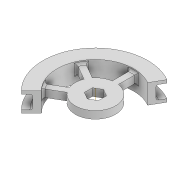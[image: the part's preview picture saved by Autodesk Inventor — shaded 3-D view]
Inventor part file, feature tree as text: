
AUTODESK INVENTOR PART (.ipt)
format: ipt  version: 2022 (Build 260153000, 153)  size: 238,080 bytes
history: native  units: mm
features: extrude x7, sketch x7, projected_geometry x4, fillet x2
ambient origin geometry x8: Origin, YZ Plane, XZ Plane, XY Plane, X Axis, Y Axis, Z Axis, Center Point
bodies: Solid1 (feature_tree)
feature tree (20):
  extrude  "Extrusion1"  Depth=44.0mm
  extrude  "Extrusion4"  Depth=4.0mm
  extrude  "Extrusion10"  Depth=1.5mm TaperAngle=0.0deg
  extrude  "Extrusion5"  Depth=20.0mm
  extrude  "Extrusion7"  Depth=1.5mm
  extrude  "Extrusion8"  Depth=10.0mm TaperAngle=0.0deg
  fillet  "Fillet1"  Radius=7.0mm
  extrude  "Extrusion9"  Depth=1.0mm
  fillet  "Fillet2"  [1 undecoded]
  sketch  "Sketch1"  dims[d0=4.1mm d1=44.0mm]
  sketch  "Sketch5"  dims[d2=3.7mm d3=0.0mm d11=4.0mm]
  projected_geometry  "Projected Loop4"
  sketch  "Sketch6"  dims[d12=1.5mm d13=0.0mm d15=1.5mm d16=0.0mm]
  projected_geometry  "Projected Loop5"
  sketch  "Sketch7"  dims[d17=3.0mm d19=20.0mm]
  projected_geometry  "Projected Loop6"
  sketch  "Sketch8"  dims[d20=3.0mm d21=1.5mm]
  sketch  "Sketch9"  dims[d24=60.0mm d26=360.0deg d28=10.0mm d29=0.0mm d30=7.0mm]
  sketch  "Sketch11"  dims[d31=10.0mm d32=0.0mm d33=1.0mm d34=150.0deg d35=45.0deg d36=10.0mm d37=0.0mm d38=3.0mm d39=3.0mm d40=0.0mm d41=20.0mm d42=1.0mm]
  projected_geometry  "Projected Loop7"
note: 1 required parameter value undecoded (feature->parameter linkage not recoverable at this tier; creation-order binding heuristic only, values carry confidence <= 0.55)
